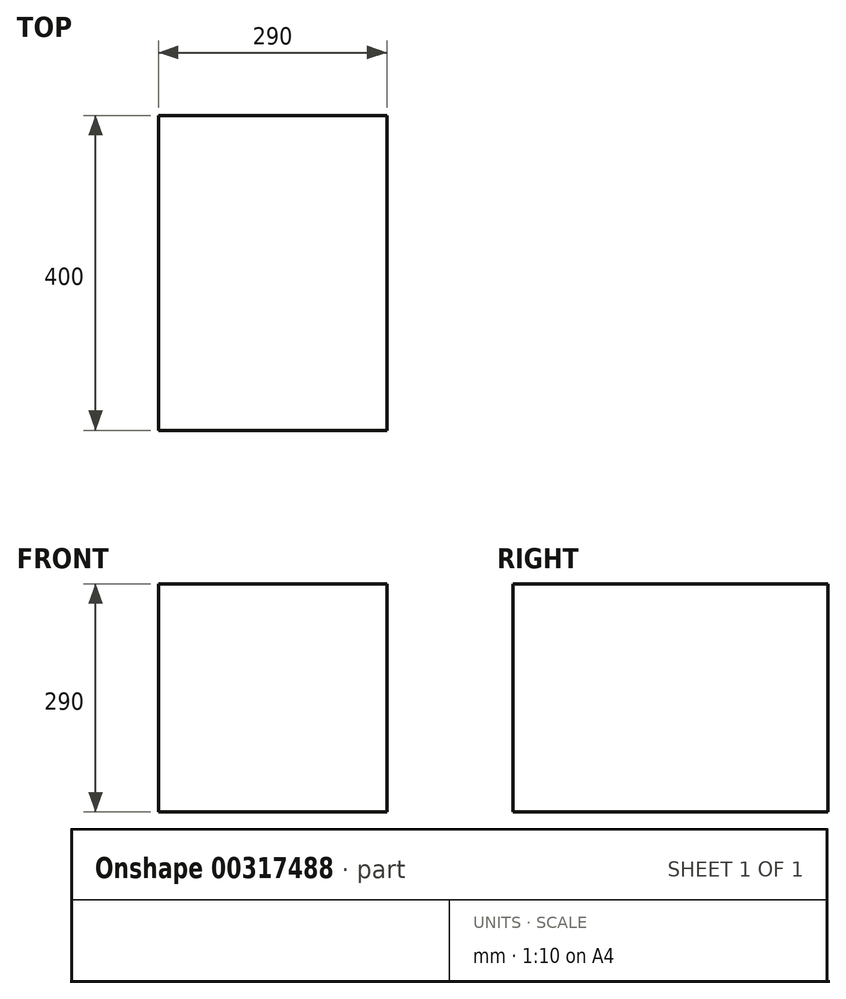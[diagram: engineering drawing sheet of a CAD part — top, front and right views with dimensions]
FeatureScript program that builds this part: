
annotation { "Feature Type Name" : "Feature", "Feature Type Description" : "" }
export const myFeature = defineFeature(function(context is Context, id is Id, definition is map)
    precondition{}
    {
        {
            var Q0;
            Q0=qCreatedBy(makeId("Front.planeOp"),FACE);
            var sketch = newSketch(context, id + "F0", { "sketchPlane" : qUnion([Q0])});
            skLineSegment(sketch, "E0.bottom", {"start": v(145, -145) * mm, "end": v(-145, -145) * mm});
            skLineSegment(sketch, "E0.top", {"start": v(145, 145) * mm, "end": v(-145, 145) * mm});
            skLineSegment(sketch, "E0.left", {"start": v(145, -145) * mm, "end": v(145, 145) * mm});
            skLineSegment(sketch, "E0.right", {"start": v(-145, -145) * mm, "end": v(-145, 145) * mm});
            skPoint(sketch, "E0.middle", {"position": v(0, 0) * mm});
            skSolve(sketch);
        }
        {
            var Q0;
            Q0 = qSketchRegion(id + "F0", true);
            extrude(context, id + "F1", {"entities" : qUnion([Q0]), "depth" : 400 * mm});
        }
    });
